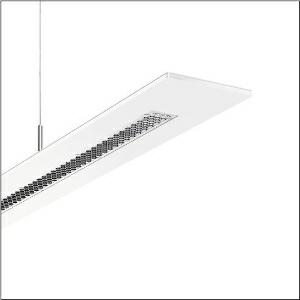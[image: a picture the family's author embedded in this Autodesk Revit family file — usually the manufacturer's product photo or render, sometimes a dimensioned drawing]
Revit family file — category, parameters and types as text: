
# Revit family: arktika_r__21_5mb251dl30830_c5c6
name_source: partatom
category: Lighting Fixtures
units: mm (PartAtom-declared; Revit-internal decimal feet)

## family parameters
Cut with Voids When Loaded = No
Host = Face
Light Source = No
Part Type = Normal
Room Calculation Point = No
Round Connector Dimension = Use Diameter
Shared = No

## types (1)
- --- (1 x LED 3000K / CRI = 80 (unbekannt), 4050 lm, 3000K)
    Apparent Load = 34 VA
    CIE Flux Codes = 81 100 100 79 100
    Color Rendering = 80
    Color Temperature = 3000K
    Default Elevation = 1800 mm
    Description = Arktika® 21, office luminaire, primary anti-glare with honeycomb louvre, of plastic, aluminium vaporised, highly specular, light emission: direct/indirect distribution, primary light characteristic: symmetric, installation type: suspended mounting, LED rated luminous flux: 4.050 lm, light colour: 830, colour temperature: 3000K, control gear: ECG DALI, with terminal, 3+2-pole, max. 2.5mm², mains connection: 220..240V, AC, 50/60Hz, rated input power: 34W, housing, of aluminium, powder-coated, traffic white (RAL 9016), 1-length, length: 1.250 mm, width: 120 mm, height: 8mm, protection rating (complete): IP20, insulation class (complete): insulation class II (safety insulation), certification: CE, ENEC, VDE, packaging unit: 1 piece
    Height = 8 mm  [stored 0.0262467 ft]
    Lamp = 1 x LED 3000K / CRI >= 80 (unbekannt)
    Lamp Light Flux = 4050 lm
    Lamp count = 1
    Length = 1250 mm
    Luminous efficacy = 120 lm/W
    Manufacturer = Siteco
    ModVariant = No
    Model = 5MB251DL30830
    Mounting Place = Ceiling
    Mounting Type = Pendant
    Number of Poles = 1
    OnlyDefault = Yes
    Power Factor = 1
    Product Name = Arktika® 21
    Product group = office luminaire | ceiling pendant
    ProductGroupID = 905
    Protection Class = Protection class II
    Protection Degree = IP 20
    RLX_Detail_Level = 1
    RlxData = <blob elided: 39345 chars, md5=939d842d>
    Socket = socket
    Standby Power = 0 W
    System Light Flux = 4050 lm
    System Power = 34 W
    Type Comments = factory setting: luminous flux: 100 % | dim-lin: 254 | 665 mA
    Type Image = l_1006128.jpg
    URL = http://relux.com
    VarID = @adj_145913
    Voltage = 0 V
    Weight = 0.00 kg
    Width = 120 mm

note: [stored X ft] marks values corroborated as IEEE doubles in the binary element streams (Revit-internal decimal feet)

## geometry (parser evidence)
native form markers: Blend x4, Sweep x12
no freeform markers — native parametric forms only
